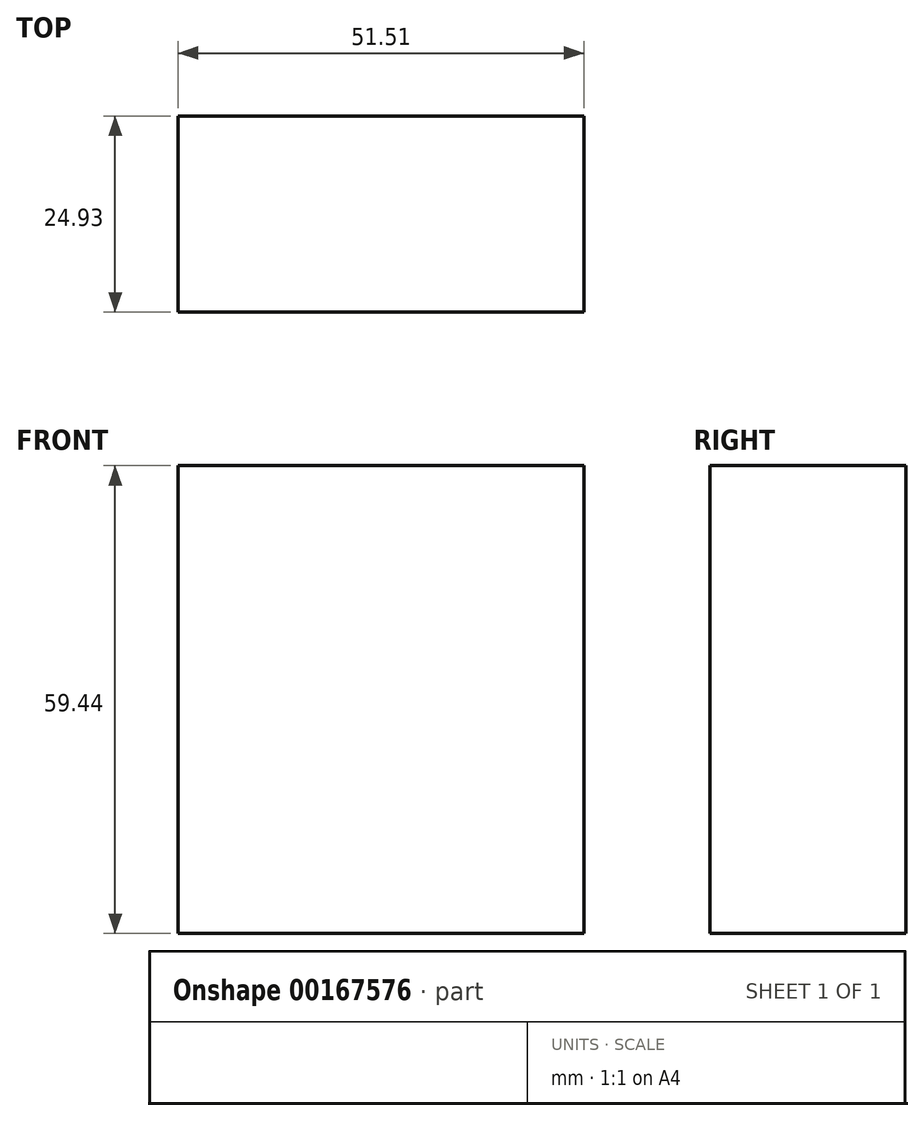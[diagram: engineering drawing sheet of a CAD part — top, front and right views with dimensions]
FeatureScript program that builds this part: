
annotation { "Feature Type Name" : "Feature", "Feature Type Description" : "" }
export const myFeature = defineFeature(function(context is Context, id is Id, definition is map)
    precondition{}
    {
        {
            var Q0;
            Q0=qCreatedBy(makeId("Top.planeOp"),FACE);
            var sketch = newSketch(context, id + "F0", { "sketchPlane" : qUnion([Q0])});
            skLineSegment(sketch, "E0.bottom", {"start": v(103.08, -64.09) * mm, "end": v(51.57, -64.09) * mm});
            skLineSegment(sketch, "E0.top", {"start": v(103.08, -39.16) * mm, "end": v(51.57, -39.16) * mm});
            skLineSegment(sketch, "E0.left", {"start": v(103.08, -64.09) * mm, "end": v(103.08, -39.16) * mm});
            skLineSegment(sketch, "E0.right", {"start": v(51.57, -64.09) * mm, "end": v(51.57, -39.16) * mm});
            skSolve(sketch);
        }
        {
            var Q0;
            Q0 = qSketchRegion(id + "F0", true);
            extrude(context, id + "F1", {"entities" : qUnion([Q0]), "depth" : 59.44 * mm});
        }
    });
